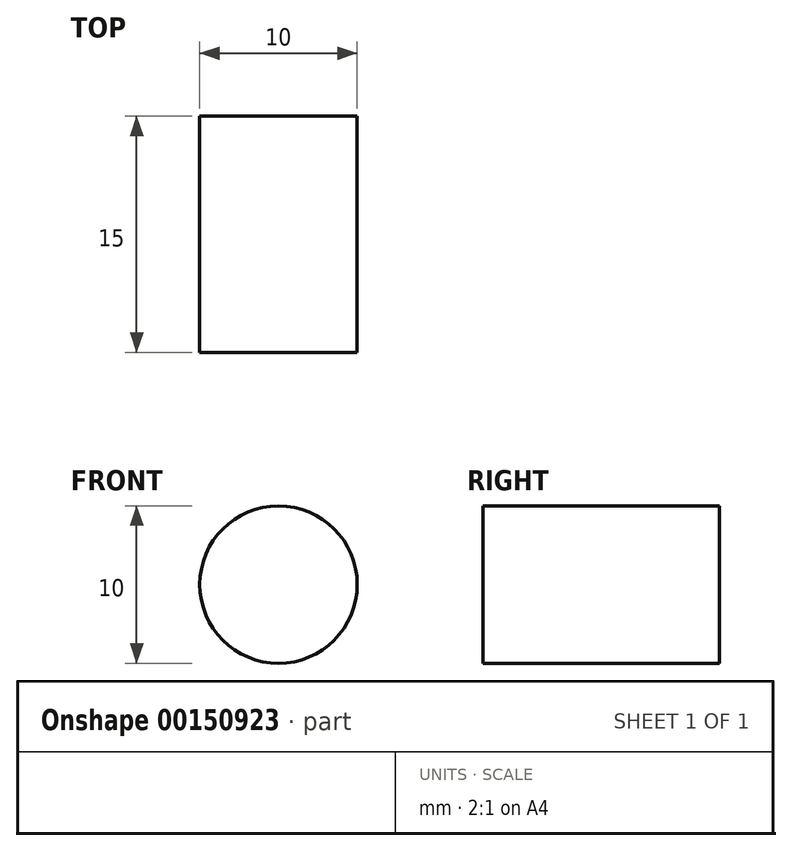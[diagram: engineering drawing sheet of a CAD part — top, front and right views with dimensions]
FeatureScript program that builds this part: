
annotation { "Feature Type Name" : "Feature", "Feature Type Description" : "" }
export const myFeature = defineFeature(function(context is Context, id is Id, definition is map)
    precondition{}
    {
        {
            var Q0;
            Q0=qCreatedBy(makeId("Front.planeOp"),FACE);
            var sketch = newSketch(context, id + "F0", { "sketchPlane" : qUnion([Q0])});
            skCircle(sketch, "E0", {"center": v(0, 0) * mm, "radius": 5 * mm});
            skSolve(sketch);
        }
        {
            var Q0;
            Q0=makeQuery(id+"F0.imprint","IMPRINT",FACE,{"disambiguationData":[TD([[makeQuery(id+"F0.imprint","IMPRINT",EDGE,{"derivedFrom":sQuery(id+"F0.wireOp",EDGE,"E0")}),1.0]])]});
            var Q1;
            Q1=sQuery(id+"F0.wireOp",EDGE,"E0");
            extrude(context, id + "F1", {"entities" : qUnion([Q0]), "surfaceEntities" : qUnion([Q1]), "depth" : 15 * mm});
        }
    });
